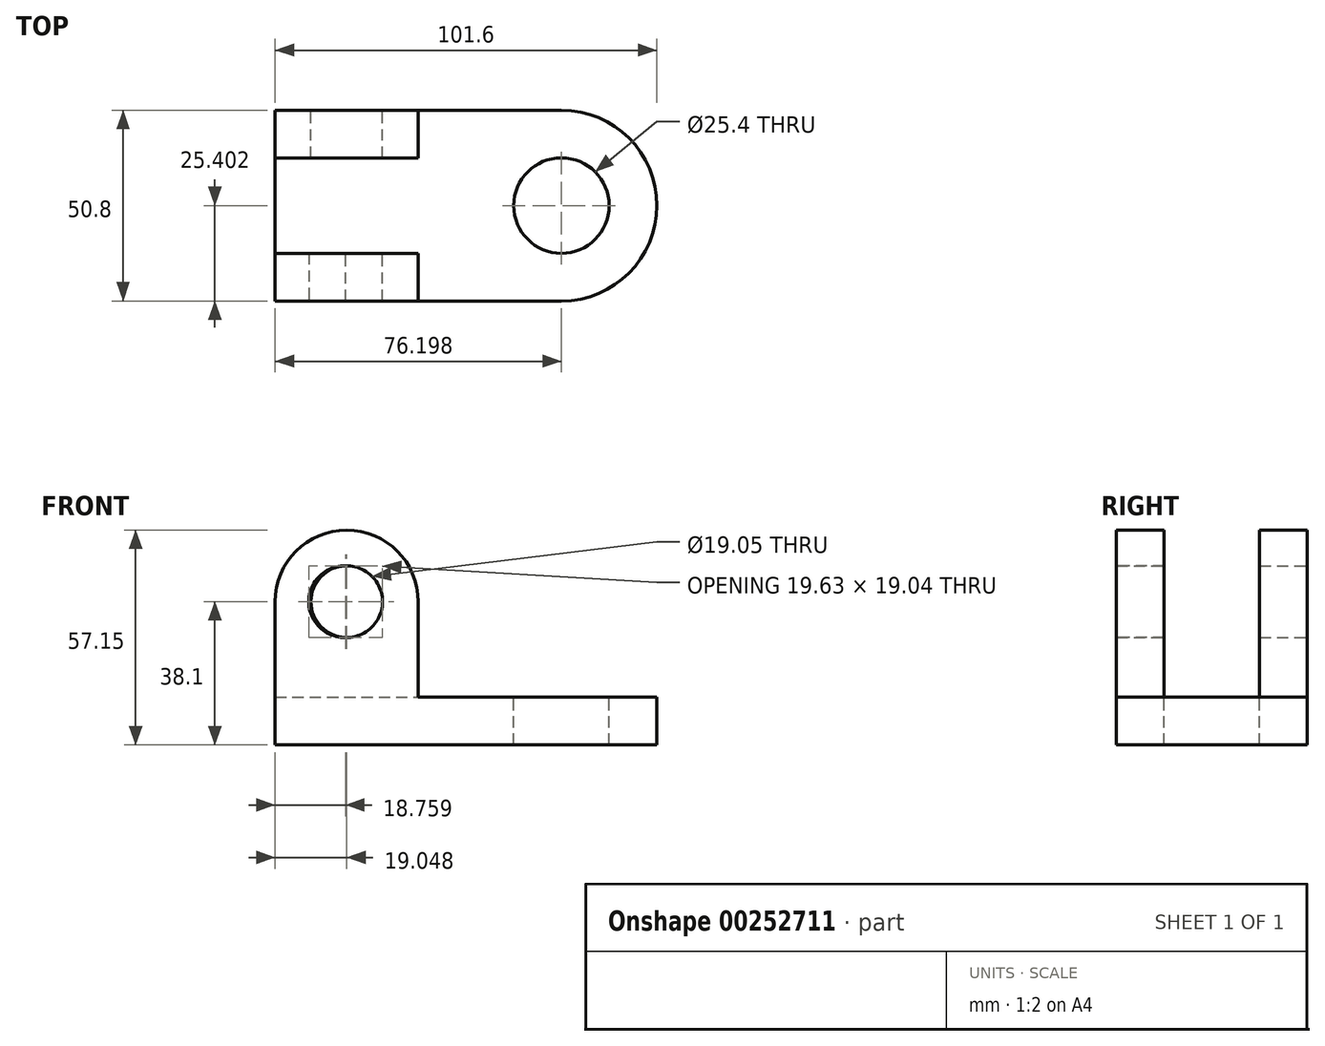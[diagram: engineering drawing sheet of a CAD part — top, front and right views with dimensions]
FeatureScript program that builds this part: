
annotation { "Feature Type Name" : "Feature", "Feature Type Description" : "" }
export const myFeature = defineFeature(function(context is Context, id is Id, definition is map)
    precondition{}
    {
        {
            var Q0;
            Q0=qCreatedBy(makeId("Top.planeOp"),FACE);
            var sketch = newSketch(context, id + "F0", { "sketchPlane" : qUnion([Q0])});
            skLineSegment(sketch, "E0", {"start": v(-38.86, -26.95) * mm, "end": v(62.74, -26.95) * mm});
            skLineSegment(sketch, "E1", {"start": v(62.74, -26.95) * mm, "end": v(62.74, 23.85) * mm});
            skLineSegment(sketch, "E2", {"start": v(62.74, 23.85) * mm, "end": v(-38.86, 23.85) * mm});
            skLineSegment(sketch, "E3", {"start": v(-38.86, 23.85) * mm, "end": v(-38.86, -26.95) * mm});
            skSolve(sketch);
        }
        {
            var Q0;
            Q0=makeQuery(id+"F0.imprint","IMPRINT",FACE,{"disambiguationData":[TD([[makeQuery(id+"F0.imprint","IMPRINT",EDGE,{"derivedFrom":sQuery(id+"F0.wireOp",EDGE,"E0")}),1.0]])]});
            extrude(context, id + "F1", {"entities" : qUnion([Q0]), "depth" : 12.7 * mm});
        }
        {
            var Q0;
            Q0=makeQuery(id+"F1.opExtrude","CAP_FACE",FACE,{"disambiguationData":[OSD([sQuery(id+"F0.wireOp",EDGE,"E0"),sQuery(id+"F0.wireOp",EDGE,"E1"),sQuery(id+"F0.wireOp",EDGE,"E2"),sQuery(id+"F0.wireOp",EDGE,"E3")])],"isStart":false});
            var sketch = newSketch(context, id + "F2", { "sketchPlane" : qUnion([Q0])});
            skCircle(sketch, "E4", {"center": v(37.34, -1.55) * mm, "radius": 12.7 * mm});
            skSolve(sketch);
        }
        {
            var Q0;
            Q0=makeQuery(id+"F1.opExtrude","SWEPT_EDGE",EDGE,{"disambiguationData":[OSD([sQuery(id+"F0.wireOp",EDGE,"E0"),sQuery(id+"F0.wireOp",EDGE,"E1")])]});
            var Q1;
            Q1=makeQuery(id+"F1.opExtrude","SWEPT_EDGE",EDGE,{"disambiguationData":[OSD([sQuery(id+"F0.wireOp",EDGE,"E1"),sQuery(id+"F0.wireOp",EDGE,"E2")])]});
            fillet(context, id + "F3", {"entities" : qUnion([Q0, Q1]), "radius" : 25.4 * mm, "tangentPropagation" : true, "allowEdgeOverflow" : false});
        }
        {
            var Q0;
            Q0=makeQuery(id+"F2.imprint","IMPRINT",FACE,{"disambiguationData":[TD([[makeQuery(id+"F2.imprint","IMPRINT",EDGE,{"derivedFrom":sQuery(id+"F2.wireOp",EDGE,"E4")}),1.0]])]});
            extrude(context, id + "F4", {"entities" : qUnion([Q0]), "operationType" : NewBodyOperationType.REMOVE, "endBound" : BoundingType.THROUGH_ALL, "oppositeDirection" : true, "depth" : 25.4 * mm});
        }
        {
            var Q0;
            Q0=makeQuery(id+"F1.opExtrude","CAP_FACE",FACE,{"disambiguationData":[OSD([sQuery(id+"F0.wireOp",EDGE,"E0"),sQuery(id+"F0.wireOp",EDGE,"E1"),sQuery(id+"F0.wireOp",EDGE,"E2"),sQuery(id+"F0.wireOp",EDGE,"E3")])],"isStart":false});
            var sketch = newSketch(context, id + "F5", { "sketchPlane" : qUnion([Q0])});
            skLineSegment(sketch, "E5", {"start": v(-38.86, -26.95) * mm, "end": v(-38.86, -14.25) * mm});
            skLineSegment(sketch, "E6", {"start": v(-38.86, -14.25) * mm, "end": v(-0.76, -14.25) * mm});
            skLineSegment(sketch, "E7", {"start": v(-0.76, -14.25) * mm, "end": v(-0.76, -26.95) * mm});
            skLineSegment(sketch, "E8", {"start": v(-0.76, -26.95) * mm, "end": v(-38.86, -26.95) * mm});
            skSolve(sketch);
        }
        {
            var Q0;
            Q0=makeQuery(id+"F5.imprint","IMPRINT",FACE,{"disambiguationData":[TD([[makeQuery(id+"F5.imprint","IMPRINT",EDGE,{"derivedFrom":sQuery(id+"F5.wireOp",EDGE,"E6")}),-1.0]])]});
            extrude(context, id + "F6", {"entities" : qUnion([Q0]), "operationType" : NewBodyOperationType.ADD, "depth" : 44.45 * mm});
        }
        {
            var Q0;
            Q0=makeQuery(id+"F6.opExtrude","CAP_EDGE",EDGE,{"disambiguationData":[OSD([sQuery(id+"F5.wireOp",EDGE,"E5")])],"isStart":false});
            var Q1;
            Q1=makeQuery(id+"F6.opExtrude","CAP_EDGE",EDGE,{"disambiguationData":[OSD([sQuery(id+"F5.wireOp",EDGE,"E7")])],"isStart":false});
            fillet(context, id + "F7", {"entities" : qUnion([Q0, Q1]), "radius" : 19.05 * mm, "tangentPropagation" : true, "allowEdgeOverflow" : false});
        }
        {
            var Q0;
            Q0=makeQuery(id+"F6.boolean.opBoolean","MERGE",FACE,{"derivedFrom":[makeQuery(id+"F1.opExtrude","SWEPT_FACE",FACE,{"disambiguationData":[OSD([sQuery(id+"F0.wireOp",EDGE,"E0")])]}),makeQuery(id+"F6.opExtrude","SWEPT_FACE",FACE,{"disambiguationData":[OSD([sQuery(id+"F5.wireOp",EDGE,"E8")])]})]});
            var sketch = newSketch(context, id + "F8", { "sketchPlane" : qUnion([Q0])});
            skCircle(sketch, "E9", {"center": v(-20.4, 38.1) * mm, "radius": 9.53 * mm});
            skSolve(sketch);
        }
        {
            var Q0;
            Q0=makeQuery(id+"F8.imprint","IMPRINT",FACE,{"disambiguationData":[TD([[makeQuery(id+"F8.imprint","IMPRINT",EDGE,{"derivedFrom":sQuery(id+"F8.wireOp",EDGE,"E9")}),1.0]])]});
            extrude(context, id + "F9", {"entities" : qUnion([Q0]), "operationType" : NewBodyOperationType.REMOVE, "endBound" : BoundingType.THROUGH_ALL, "oppositeDirection" : true, "depth" : 25.4 * mm});
        }
        {
            var Q0;
            Q0=makeQuery(id+"F1.opExtrude","CAP_FACE",FACE,{"disambiguationData":[OSD([sQuery(id+"F0.wireOp",EDGE,"E0"),sQuery(id+"F0.wireOp",EDGE,"E1"),sQuery(id+"F0.wireOp",EDGE,"E2"),sQuery(id+"F0.wireOp",EDGE,"E3")])],"isStart":false});
            var sketch = newSketch(context, id + "F10", { "sketchPlane" : qUnion([Q0])});
            skLineSegment(sketch, "E10", {"start": v(-0.76, 23.85) * mm, "end": v(-38.86, 23.85) * mm});
            skLineSegment(sketch, "E11", {"start": v(-38.86, 23.85) * mm, "end": v(-38.86, 11.15) * mm});
            skLineSegment(sketch, "E12", {"start": v(-38.86, 11.15) * mm, "end": v(-0.76, 11.15) * mm});
            skLineSegment(sketch, "E13", {"start": v(-0.76, 11.15) * mm, "end": v(-0.76, 23.85) * mm});
            skSolve(sketch);
        }
        {
            var Q0;
            Q0=makeQuery(id+"F10.imprint","IMPRINT",FACE,{"disambiguationData":[TD([[makeQuery(id+"F10.imprint","IMPRINT",EDGE,{"derivedFrom":sQuery(id+"F10.wireOp",EDGE,"E10")}),1.0]])]});
            extrude(context, id + "F11", {"entities" : qUnion([Q0]), "operationType" : NewBodyOperationType.ADD, "depth" : 44.45 * mm});
        }
        {
            var Q0;
            Q0=makeQuery(id+"F11.opExtrude","CAP_EDGE",EDGE,{"disambiguationData":[OSD([sQuery(id+"F10.wireOp",EDGE,"E13")])],"isStart":false});
            var Q1;
            Q1=makeQuery(id+"F11.opExtrude","CAP_EDGE",EDGE,{"disambiguationData":[OSD([sQuery(id+"F10.wireOp",EDGE,"E11")])],"isStart":false});
            fillet(context, id + "F12", {"entities" : qUnion([Q0, Q1]), "radius" : 19.05 * mm, "tangentPropagation" : true, "allowEdgeOverflow" : false});
        }
        {
            var Q0;
            Q0=makeQuery(id+"F11.boolean.opBoolean","MERGE",FACE,{"derivedFrom":[makeQuery(id+"F1.opExtrude","SWEPT_FACE",FACE,{"disambiguationData":[OSD([sQuery(id+"F0.wireOp",EDGE,"E2")])]}),makeQuery(id+"F11.opExtrude","SWEPT_FACE",FACE,{"disambiguationData":[OSD([sQuery(id+"F10.wireOp",EDGE,"E10")])]})]});
            var sketch = newSketch(context, id + "F13", { "sketchPlane" : qUnion([Q0])});
            skCircle(sketch, "E14", {"center": v(19.81, 38.1) * mm, "radius": 9.53 * mm});
            skSolve(sketch);
        }
        {
            var Q0;
            Q0=makeQuery(id+"F13.imprint","IMPRINT",FACE,{"disambiguationData":[TD([[makeQuery(id+"F13.imprint","IMPRINT",EDGE,{"derivedFrom":sQuery(id+"F13.wireOp",EDGE,"E14")}),1.0]])]});
            extrude(context, id + "F14", {"entities" : qUnion([Q0]), "operationType" : NewBodyOperationType.REMOVE, "endBound" : BoundingType.THROUGH_ALL, "oppositeDirection" : true, "depth" : 25.4 * mm});
        }
    });
